# Revit family: DC_Holyoake_LowLeakageDamper_HBD-155-MAN_13
name_source: partatom
category: Duct Accessories
revit_build: Autodesk Revit 2014 (Build: 20130308_1515(x64)
units: mm (PartAtom-declared; Revit-internal decimal feet)

## types (1)
- Variable Width & Height
    3D Visibility ON OFF = No
    Description = Manual Balancing Dampers shall be Holyoake Model HBD-155-MAN. Manual Balancing Dampers shall be of 6063 T5 extruded aluminium construction, with a 150mm Flanged Frame incorporating pre-punched corner slots for Duct Flange mounting or Channel Frame suitable for fixing inside ductwork. Manual Balancing Dampers shall be fitted with 11mm Hexagonal shafts and shall rotate in two piece Acetal self lubricating bearings. Manual Balancing Dampers shall be fitted with HCD-14 locking quadrant.
    Holyoake Product Range = Holyoake Motorised Volume Control Damper
    Manufacturer = Holyoake
    Material Body = Holyoake-Aluminium
    Material Face = Holyoake-Aluminium
    Model = HBD-155-MANUAL
    Static Pressure Max / sqm = 2000 Pa
    Static Pressure Min / sqm = 10 Pa
    Type Comments = Manual Volume Control Damper.
    URL = http://www.holyoake.com

## geometry (parser evidence)
native form markers: Blend x12, Extrusion x6, Sweep x3
no freeform markers — native parametric forms only
